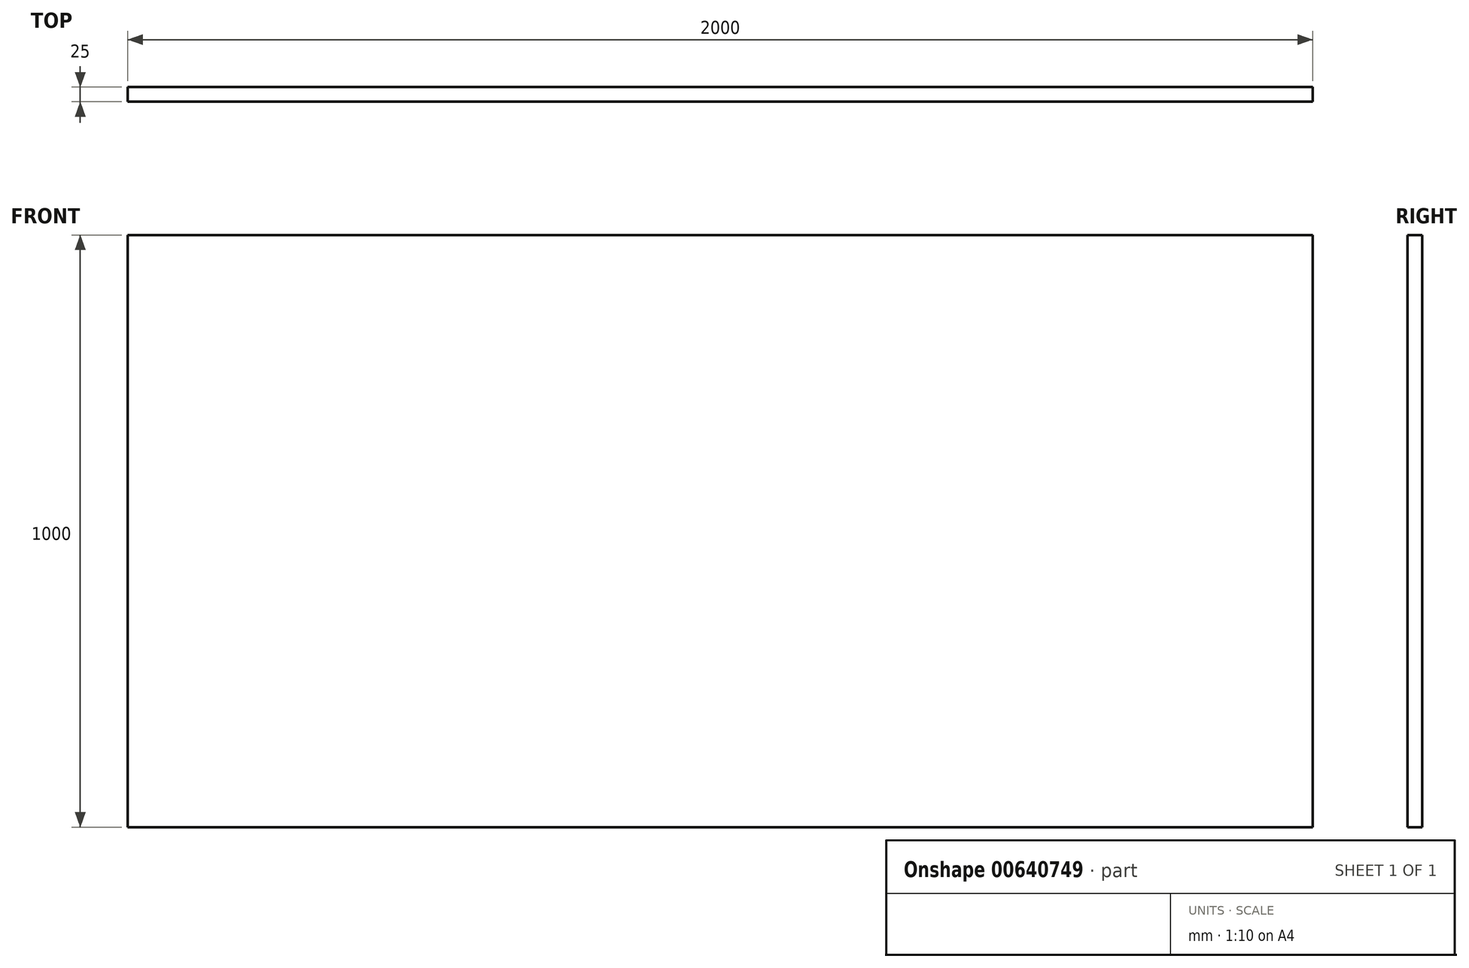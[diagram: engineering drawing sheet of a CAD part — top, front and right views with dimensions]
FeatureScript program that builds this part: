
annotation { "Feature Type Name" : "Feature", "Feature Type Description" : "" }
export const myFeature = defineFeature(function(context is Context, id is Id, definition is map)
    precondition{}
    {
        {
            var Q0;
            Q0=qCreatedBy(makeId("Front.planeOp"),FACE);
            var sketch = newSketch(context, id + "F0", { "sketchPlane" : qUnion([Q0])});
            skLineSegment(sketch, "E0.bottom", {"start": v(1000, 500) * mm, "end": v(-1000, 500) * mm});
            skLineSegment(sketch, "E0.top", {"start": v(1000, -500) * mm, "end": v(-1000, -500) * mm});
            skLineSegment(sketch, "E0.left", {"start": v(1000, 500) * mm, "end": v(1000, -500) * mm});
            skLineSegment(sketch, "E0.right", {"start": v(-1000, 500) * mm, "end": v(-1000, -500) * mm});
            skSolve(sketch);
        }
        {
            var Q0;
            Q0=makeQuery(id+"F0.imprint","IMPRINT",FACE,{"disambiguationData":[TD([[makeQuery(id+"F0.imprint","IMPRINT",EDGE,{"derivedFrom":sQuery(id+"F0.wireOp",EDGE,"E0.bottom")}),1.0]])]});
            extrude(context, id + "F1", {"entities" : qUnion([Q0]), "depth" : 25 * mm, "offsetDistance" : 25 * mm});
        }
    });
